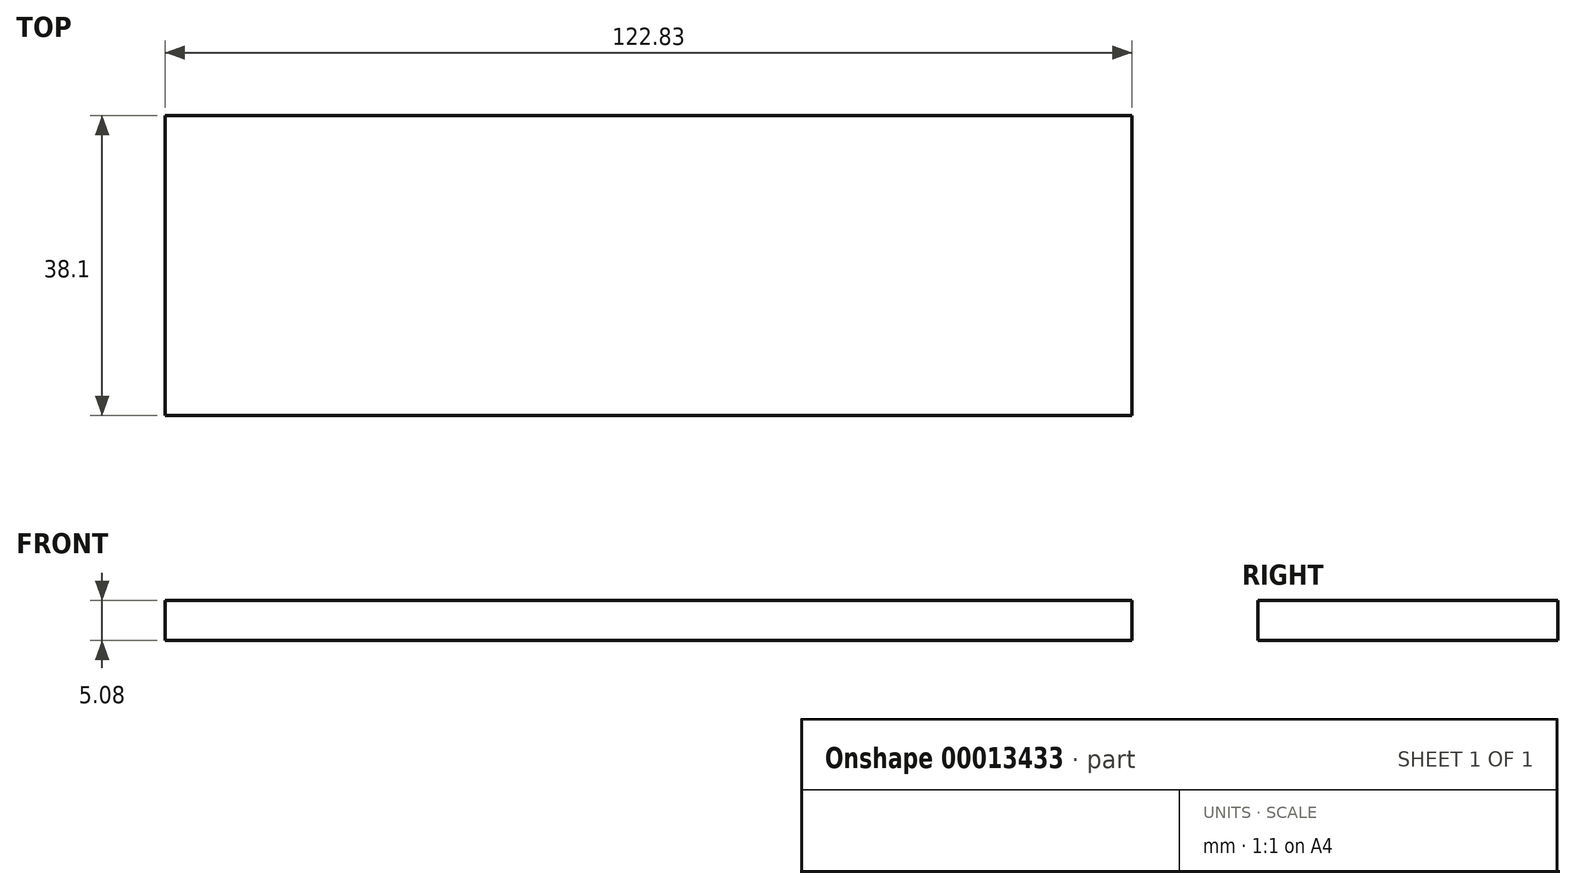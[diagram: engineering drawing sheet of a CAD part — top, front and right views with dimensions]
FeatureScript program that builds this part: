
annotation { "Feature Type Name" : "Feature", "Feature Type Description" : "" }
export const myFeature = defineFeature(function(context is Context, id is Id, definition is map)
    precondition{}
    {
        {
            var Q0;
            Q0=qCreatedBy(makeId("Top.planeOp"),FACE);
            var sketch = newSketch(context, id + "F0", { "sketchPlane" : qUnion([Q0])});
            skLineSegment(sketch, "E0.bottom", {"start": v(0, 0) * mm, "end": v(122.83, 0) * mm});
            skLineSegment(sketch, "E0.top", {"start": v(0, 38.1) * mm, "end": v(122.83, 38.1) * mm});
            skLineSegment(sketch, "E0.left", {"start": v(0, 0) * mm, "end": v(0, 38.1) * mm});
            skLineSegment(sketch, "E0.right", {"start": v(122.83, 0) * mm, "end": v(122.83, 38.1) * mm});
            skSolve(sketch);
        }
        {
            var Q0;
            Q0 = qSketchRegion(id + "F0", true);
            extrude(context, id + "F1", {"entities" : qUnion([Q0]), "depth" : 5.08 * mm});
        }
    });
